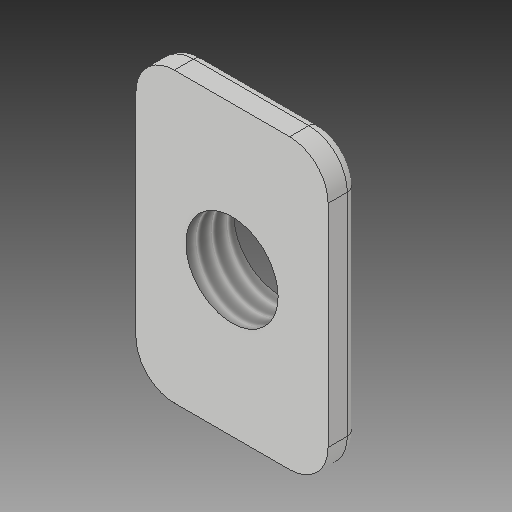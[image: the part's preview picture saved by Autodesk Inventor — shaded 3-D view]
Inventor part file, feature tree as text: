
AUTODESK INVENTOR PART (.ipt)
format: ipt  version: 2017 (Build 210142000, 142)  size: 157,184 bytes
history: native  units: mm
features: other x3, sketch x2
ambient origin geometry x8: Origin, YZ Plane, XZ Plane, XY Plane, X Axis, Y Axis, Z Axis, Center Point
bodies: Solid1 (feature_tree)
feature tree (5):
  other  "M5 Tee Nut-Generic.ipt"
  other  "Solid1::M5 Tee Nut-Generic.ipt"
  other  "TaggingFeature1"
  sketch  "Sketch1"  dims[d0=10.0mm]
  sketch  "Sketch2"
